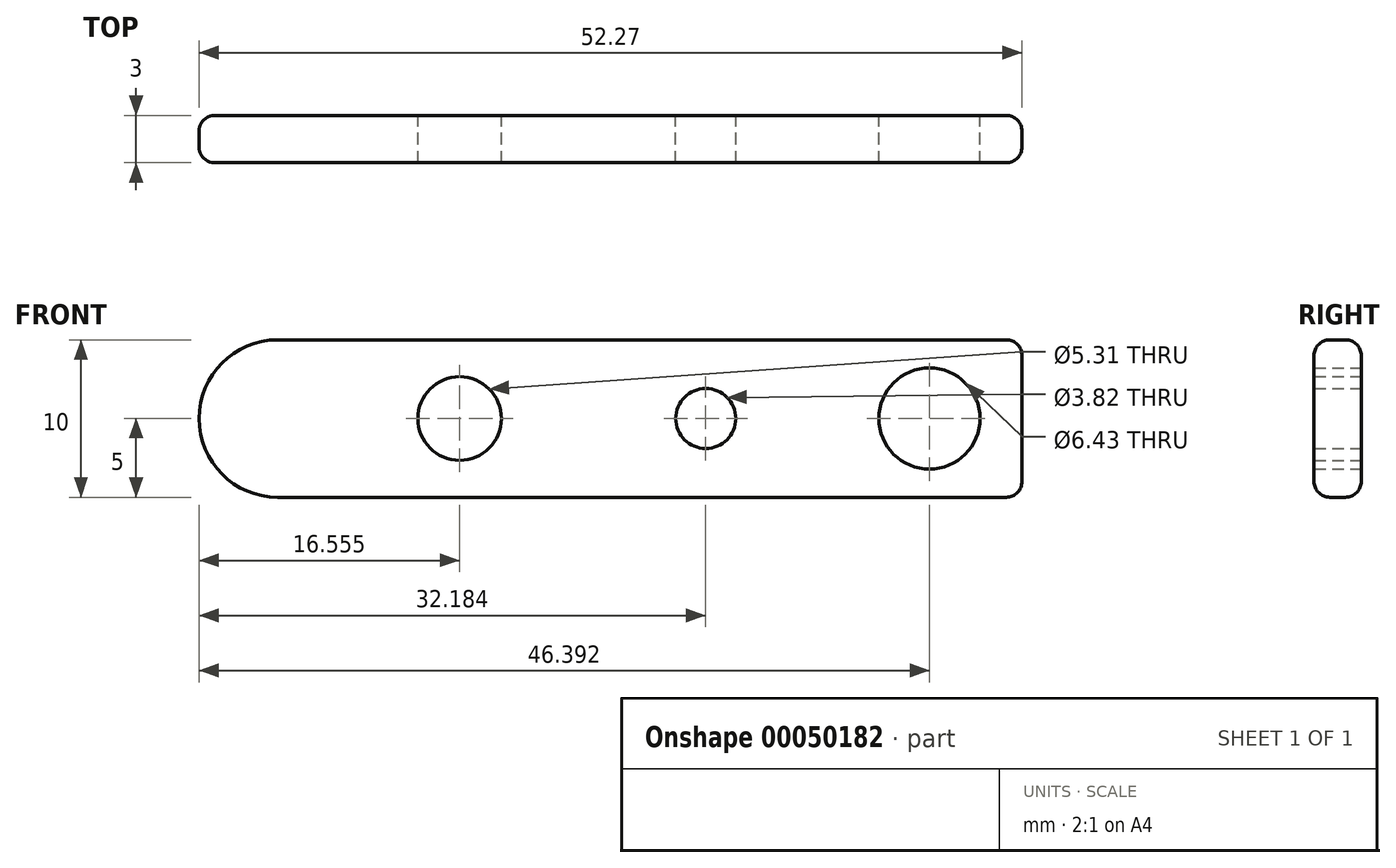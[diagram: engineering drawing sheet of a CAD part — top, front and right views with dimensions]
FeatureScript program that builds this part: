
annotation { "Feature Type Name" : "Feature", "Feature Type Description" : "" }
export const myFeature = defineFeature(function(context is Context, id is Id, definition is map)
    precondition{}
    {
        {
            var Q0;
            Q0=qCreatedBy(makeId("Front.planeOp"),FACE);
            var sketch = newSketch(context, id + "F0", { "sketchPlane" : qUnion([Q0])});
            skLineSegment(sketch, "E0", {"start": v(5, 0) * mm, "end": v(52.27, 0) * mm});
            skLineSegment(sketch, "E1", {"start": v(52.27, 0) * mm, "end": v(52.27, 10) * mm});
            skLineSegment(sketch, "E2", {"start": v(52.27, 10) * mm, "end": v(5, 10) * mm});
            skLineSegment(sketch, "E3", {"start": v(0, 5) * mm, "end": v(0, 5) * mm});
            skArc(sketch, "E4.filletArc", {"start": v(5, 10) * mm, "mid": v(1.46, 8.54) * mm, "end": v(0, 5) * mm});
            skArc(sketch, "E5.filletArc", {"start": v(0, 5) * mm, "mid": v(1.46, 1.46) * mm, "end": v(5, 0) * mm});
            skCircle(sketch, "E6", {"center": v(16.55, 5) * mm, "radius": 2.65 * mm});
            skCircle(sketch, "E7", {"center": v(32.18, 5) * mm, "radius": 1.9 * mm});
            skCircle(sketch, "E8", {"center": v(46.4, 5) * mm, "radius": 3.21 * mm});
            skSolve(sketch);
        }
        {
            var Q0;
            Q0=makeQuery(id+"F0.imprint","IMPRINT",FACE,{"disambiguationData":[TD([[makeQuery(id+"F0.imprint","IMPRINT",EDGE,{"derivedFrom":sQuery(id+"F0.wireOp",EDGE,"E0")}),1.0]])]});
            extrude(context, id + "F1", {"entities" : qUnion([Q0]), "depth" : 3 * mm});
        }
        {
            var Q0;
            Q0=makeQuery(id+"F1.opExtrude","SWEPT_FACE",FACE,{"disambiguationData":[OSD([sQuery(id+"F0.wireOp",EDGE,"E2")])]});
            var Q1;
            Q1=makeQuery(id+"F1.opExtrude","SWEPT_FACE",FACE,{"disambiguationData":[OSD([sQuery(id+"F0.wireOp",EDGE,"E1")])]});
            fillet(context, id + "F2", {"entities" : qUnion([Q0, Q1]), "radius" : 1 * mm, "tangentPropagation" : true, "allowEdgeOverflow" : false});
        }
    });
